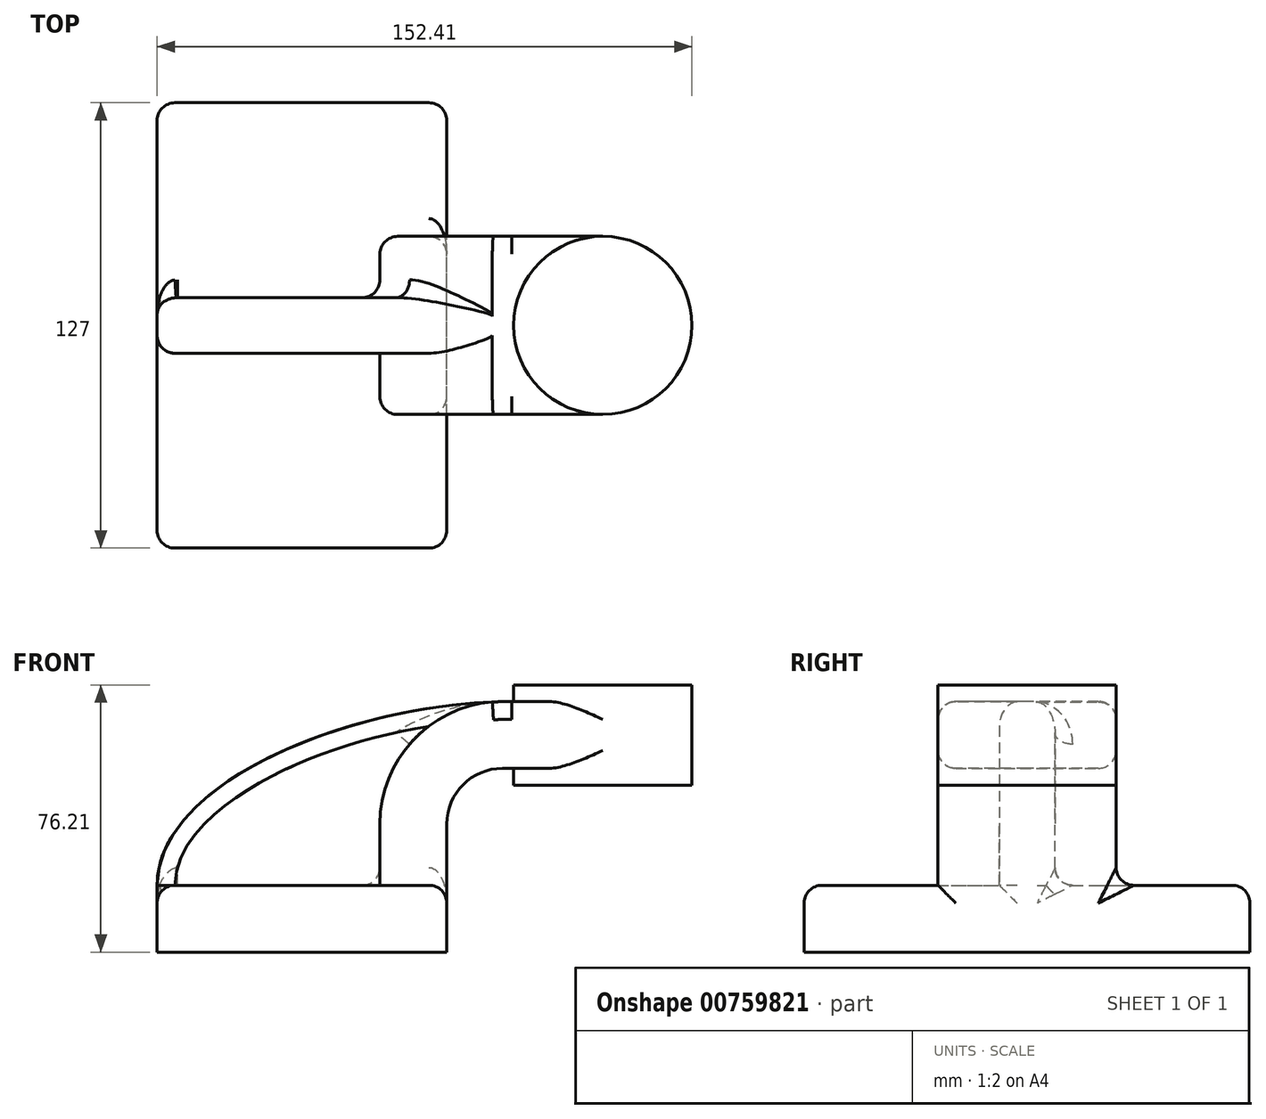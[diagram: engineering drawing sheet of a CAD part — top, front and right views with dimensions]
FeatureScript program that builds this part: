
annotation { "Feature Type Name" : "Feature", "Feature Type Description" : "" }
export const myFeature = defineFeature(function(context is Context, id is Id, definition is map)
    precondition{}
    {
        {
            var Q0;
            Q0=qCreatedBy(makeId("Front.planeOp"),FACE);
            var sketch = newSketch(context, id + "F0", { "sketchPlane" : qUnion([Q0])});
            skLineSegment(sketch, "E0.bottom", {"start": v(41.27, 9.53) * mm, "end": v(-41.28, 9.53) * mm});
            skLineSegment(sketch, "E0.top", {"start": v(41.28, -9.52) * mm, "end": v(-41.27, -9.52) * mm});
            skLineSegment(sketch, "E0.left", {"start": v(41.28, 9.53) * mm, "end": v(41.28, -9.52) * mm});
            skLineSegment(sketch, "E0.right", {"start": v(-41.28, 9.53) * mm, "end": v(-41.27, -9.52) * mm});
            skPoint(sketch, "E0.middle", {"position": v(0, 0) * mm});
            skLineSegment(sketch, "E1.bottom", {"start": v(111.12, 38.1) * mm, "end": v(60.32, 38.1) * mm});
            skLineSegment(sketch, "E1.top", {"start": v(111.12, 66.68) * mm, "end": v(60.32, 66.68) * mm});
            skLineSegment(sketch, "E1.left", {"start": v(111.12, 38.1) * mm, "end": v(111.12, 66.68) * mm});
            skLineSegment(sketch, "E1.right", {"start": v(60.32, 38.1) * mm, "end": v(60.32, 66.68) * mm});
            skPoint(sketch, "E1.middle", {"position": v(85.72, 52.39) * mm});
            skLineSegment(sketch, "E2", {"start": v(41.27, 9.53) * mm, "end": v(41.27, 27) * mm});
            skArc(sketch, "E3", {"start": v(41.27, 27) * mm, "mid": v(45.92, 38.23) * mm, "end": v(57.15, 42.88) * mm});
            skLineSegment(sketch, "E4", {"start": v(57.15, 42.88) * mm, "end": v(85.72, 42.88) * mm});
            skLineSegment(sketch, "E5.0", {"start": v(57.15, 61.93) * mm, "end": v(85.72, 61.93) * mm});
            skArc(sketch, "E5.1", {"start": v(22.23, 27) * mm, "mid": v(32.45, 51.7) * mm, "end": v(57.15, 61.93) * mm});
            skLineSegment(sketch, "E5.2", {"start": v(22.22, 9.53) * mm, "end": v(22.22, 27) * mm});
            skFitSpline(sketch, "E6", {"points": [v(-41.28, 9.53) * mm, v(60.32, 61.93) * mm], "startDerivative": vector(-0.32, 88.5) * mm, "endDerivative": vector(136.45, -0.3) * mm});
            skPoint(sketch, "E7", {"position": v(85.72, 66.68) * mm});
            skLineSegment(sketch, "E8", {"start": v(85.72, 38.1) * mm, "end": v(85.72, 66.68) * mm});
            skSolve(sketch);
        }
        {
            var Q0;
            Q0=makeQuery(id+"F0.imprint","IMPRINT",FACE,{"disambiguationData":[TD([[makeQuery(id+"F0.imprint","IMPRINT",EDGE,{"derivedFrom":sQuery(id+"F0.wireOp",EDGE,"E0.top")}),-1.0]])]});
            extrude(context, id + "F1", {"entities" : qUnion([Q0]), "endBound" : BoundingType.SYMMETRIC, "depth" : 127 * mm, "offsetDistance" : 25.4 * mm});
        }
        {
            var Q0;
            {var subQ3=sQuery(id+"F0.wireOp",EDGE,"E5.2");Q0=makeQuery(id+"F0.imprint","IMPRINT",FACE,{"disambiguationData":[TD([[makeQuery(id+"F0.imprint","IMPRINT",EDGE,{"derivedFrom":subQ3}),1.0]])]});}
            extrude(context, id + "F2", {"entities" : qUnion([Q0]), "operationType" : NewBodyOperationType.ADD, "endBound" : BoundingType.SYMMETRIC, "depth" : 15.88 * mm, "offsetDistance" : 25.4 * mm});
        }
        {
            var Q0;
            {var subQ1=sQuery(id+"F0.wireOp",EDGE,"E2");Q0=makeQuery(id+"F0.imprint","IMPRINT",FACE,{"disambiguationData":[TD([[makeQuery(id+"F0.imprint","IMPRINT",EDGE,{"derivedFrom":subQ1}),1.0]])]});}
            var Q1;
            {var subQ3=sQuery(id+"F0.wireOp",EDGE,"E4");var subQ5=sQuery(id+"F0.wireOp",EDGE,"E8");var subQ6=makeQuery(id+"F0.imprint","INTERSECT",VERTEX,{"derivedFrom":[subQ3,subQ5]});Q1=makeQuery(id+"F0.imprint","IMPRINT",FACE,{"disambiguationData":[TD([[makeQuery(id+"F0.imprint","IMPRINT",EDGE,{"disambiguationData":[TD([[subQ6,1.0]])],"derivedFrom":subQ3}),1.0]])]});}
            extrude(context, id + "F3", {"entities" : qUnion([Q0, Q1]), "operationType" : NewBodyOperationType.ADD, "endBound" : BoundingType.SYMMETRIC, "depth" : 50.8 * mm, "offsetDistance" : 25.4 * mm});
        }
        {
            var Q0;
            {var subQ0=sQuery(id+"F0.wireOp",EDGE,"E1.left");Q0=makeQuery(id+"F0.imprint","IMPRINT",FACE,{"disambiguationData":[TD([[makeQuery(id+"F0.imprint","IMPRINT",EDGE,{"derivedFrom":subQ0}),1.0]])]});}
            var Q1;
            Q1=sQuery(id+"F0.wireOp",EDGE,"E8");
            revolve(context, id + "F4", {"operationType" : NewBodyOperationType.ADD, "surfaceOperationType" : NewSurfaceOperationType.NEW, "entities" : qUnion([Q0]), "axis" : qUnion([Q1]), "revolveType" : RevolveType.FULL});
        }
        {
            var Q0;
            Q0=makeQuery(id+"F1.opExtrude","CAP_EDGE",EDGE,{"disambiguationData":[OSD([sQuery(id+"F0.wireOp",EDGE,"E0.right")])],"isStart":true});
            var Q1;
            Q1=makeQuery(id+"F1.opExtrude","CAP_EDGE",EDGE,{"disambiguationData":[OSD([sQuery(id+"F0.wireOp",EDGE,"E0.left")])],"isStart":true});
            var Q2;
            Q2=makeQuery(id+"F1.opExtrude","CAP_EDGE",EDGE,{"disambiguationData":[OSD([sQuery(id+"F0.wireOp",EDGE,"E0.right")])],"isStart":false});
            var Q3;
            Q3=makeQuery(id+"F1.opExtrude","CAP_EDGE",EDGE,{"disambiguationData":[OSD([sQuery(id+"F0.wireOp",EDGE,"E0.left")])],"isStart":false});
            var Q4;
            Q4=makeQuery(id+"F1.opExtrude","CAP_EDGE",EDGE,{"disambiguationData":[OSD([sQuery(id+"F0.wireOp",EDGE,"E0.bottom")])],"isStart":false});
            var Q5;
            {var subQ0=sQuery(id+"F0.wireOp",EDGE,"E0.left");var subQ1=sQuery(id+"F0.wireOp",EDGE,"E2");var subQ2=sQuery(id+"F0.wireOp",EDGE,"E0.bottom");Q5=makeQuery(id+"F3.boolean.opBoolean","SPLIT",EDGE,{"disambiguationData":[TD([makeQuery(id+"F1.opExtrude","CAP_FACE",FACE,{"disambiguationData":[OSD([subQ2,sQuery(id+"F0.wireOp",EDGE,"E0.top"),subQ0,sQuery(id+"F0.wireOp",EDGE,"E0.right")])],"isStart":false})])],"derivedFrom":makeQuery(id+"F1.opExtrude","SWEPT_EDGE",EDGE,{"disambiguationData":[OSD([subQ2,subQ0,subQ1])]})});}
            var Q6;
            {var subQ0=sQuery(id+"F0.wireOp",EDGE,"E6");var subQ1=sQuery(id+"F0.wireOp",EDGE,"E0.bottom");var subQ2=sQuery(id+"F0.wireOp",EDGE,"E0.right");Q6=makeQuery(id+"F2.boolean.opBoolean","SPLIT",EDGE,{"disambiguationData":[TD([makeQuery(id+"F1.opExtrude","CAP_FACE",FACE,{"disambiguationData":[OSD([subQ1,sQuery(id+"F0.wireOp",EDGE,"E0.top"),sQuery(id+"F0.wireOp",EDGE,"E0.left"),subQ2])],"isStart":false})])],"derivedFrom":makeQuery(id+"F1.opExtrude","SWEPT_EDGE",EDGE,{"disambiguationData":[OSD([subQ1,subQ2,subQ0])]})});}
            var Q7;
            {var subQ0=sQuery(id+"F0.wireOp",EDGE,"E6");var subQ1=sQuery(id+"F0.wireOp",EDGE,"E0.bottom");var subQ2=sQuery(id+"F0.wireOp",EDGE,"E0.right");Q7=makeQuery(id+"F2.boolean.opBoolean","SPLIT",EDGE,{"disambiguationData":[TD([makeQuery(id+"F1.opExtrude","CAP_FACE",FACE,{"disambiguationData":[OSD([subQ1,sQuery(id+"F0.wireOp",EDGE,"E0.top"),sQuery(id+"F0.wireOp",EDGE,"E0.left"),subQ2])],"isStart":true})])],"derivedFrom":makeQuery(id+"F1.opExtrude","SWEPT_EDGE",EDGE,{"disambiguationData":[OSD([subQ1,subQ2,subQ0])]})});}
            var Q8;
            Q8=makeQuery(id+"F1.opExtrude","CAP_EDGE",EDGE,{"disambiguationData":[OSD([sQuery(id+"F0.wireOp",EDGE,"E0.bottom")])],"isStart":true});
            var Q9;
            {var subQ0=sQuery(id+"F0.wireOp",EDGE,"E2");var subQ1=sQuery(id+"F0.wireOp",EDGE,"E0.bottom");var subQ2=sQuery(id+"F0.wireOp",EDGE,"E0.left");Q9=makeQuery(id+"F3.boolean.opBoolean","SPLIT",EDGE,{"disambiguationData":[TD([makeQuery(id+"F1.opExtrude","CAP_FACE",FACE,{"disambiguationData":[OSD([subQ1,sQuery(id+"F0.wireOp",EDGE,"E0.top"),subQ2,sQuery(id+"F0.wireOp",EDGE,"E0.right")])],"isStart":true})])],"derivedFrom":makeQuery(id+"F1.opExtrude","SWEPT_EDGE",EDGE,{"disambiguationData":[OSD([subQ1,subQ2,subQ0])]})});}
            fillet(context, id + "F5", {"entities" : qUnion([Q0, Q1, Q2, Q3, Q4, Q5, Q6, Q7, Q8, Q9]), "radius" : 5.08 * mm, "tangentPropagation" : true, "allowEdgeOverflow" : false});
        }
        {
            var Q0;
            Q0=makeQuery(id+"F2.opExtrude","CAP_EDGE",EDGE,{"disambiguationData":[OSD([sQuery(id+"F0.wireOp",EDGE,"E6")])],"isStart":true});
            var Q1;
            Q1=makeQuery(id+"F2.opExtrude","CAP_EDGE",EDGE,{"disambiguationData":[OSD([sQuery(id+"F0.wireOp",EDGE,"E6")])],"isStart":false});
            var Q2;
            Q2=makeQuery(id+"F3.opExtrude","CAP_EDGE",EDGE,{"disambiguationData":[OSD([sQuery(id+"F0.wireOp",EDGE,"E5.1")])],"isStart":false});
            var Q3;
            Q3=makeQuery(id+"F3.opExtrude","CAP_EDGE",EDGE,{"disambiguationData":[OSD([sQuery(id+"F0.wireOp",EDGE,"E5.0")])],"isStart":false});
            var Q4;
            Q4=makeQuery(id+"F3.opExtrude","CAP_EDGE",EDGE,{"disambiguationData":[OSD([sQuery(id+"F0.wireOp",EDGE,"E5.0")])],"isStart":true});
            var Q5;
            Q5=makeQuery(id+"F3.opExtrude","CAP_EDGE",EDGE,{"disambiguationData":[OSD([sQuery(id+"F0.wireOp",EDGE,"E5.2")])],"isStart":true});
            var Q6;
            Q6=makeQuery(id+"F3.opExtrude","CAP_EDGE",EDGE,{"disambiguationData":[OSD([sQuery(id+"F0.wireOp",EDGE,"E2")])],"isStart":true});
            var Q7;
            Q7=makeQuery(id+"F3.opExtrude","CAP_EDGE",EDGE,{"disambiguationData":[OSD([sQuery(id+"F0.wireOp",EDGE,"E2")])],"isStart":false});
            fillet(context, id + "F6", {"entities" : qUnion([Q0, Q1, Q2, Q3, Q4, Q5, Q6, Q7]), "radius" : 5.08 * mm, "tangentPropagation" : true, "allowEdgeOverflow" : false});
        }
        {
            var Q0;
            Q0=makeQuery(id+"F2.opExtrude","CAP_EDGE",EDGE,{"disambiguationData":[OSD([sQuery(id+"F0.wireOp",EDGE,"E0.bottom")])],"isStart":true});
            var Q1;
            Q1=makeQuery(id+"F2.opExtrude","CAP_EDGE",EDGE,{"disambiguationData":[OSD([sQuery(id+"F0.wireOp",EDGE,"E5.1")])],"isStart":true});
            var Q2;
            Q2=makeQuery(id+"F2.opExtrude","CAP_EDGE",EDGE,{"disambiguationData":[OSD([sQuery(id+"F0.wireOp",EDGE,"E5.2")])],"isStart":false});
            var Q3;
            Q3=makeQuery(id+"F2.opExtrude","CAP_EDGE",EDGE,{"disambiguationData":[OSD([sQuery(id+"F0.wireOp",EDGE,"E0.bottom")])],"isStart":false});
            fillet(context, id + "F7", {"entities" : qUnion([Q0, Q1, Q2, Q3]), "radius" : 5.08 * mm, "tangentPropagation" : true, "allowEdgeOverflow" : false});
        }
        {
            var Q0;
            Q0=makeQuery(id+"F3.opExtrude","CAP_EDGE",EDGE,{"disambiguationData":[OSD([sQuery(id+"F0.wireOp",EDGE,"E0.bottom")])],"isStart":false});
            var Q1;
            Q1=makeQuery(id+"F3.opExtrude","CAP_EDGE",EDGE,{"disambiguationData":[OSD([sQuery(id+"F0.wireOp",EDGE,"E0.bottom")])],"isStart":true});
            fillet(context, id + "F8", {"entities" : qUnion([Q0, Q1]), "radius" : 5.08 * mm, "tangentPropagation" : true, "allowEdgeOverflow" : false});
        }
    });
